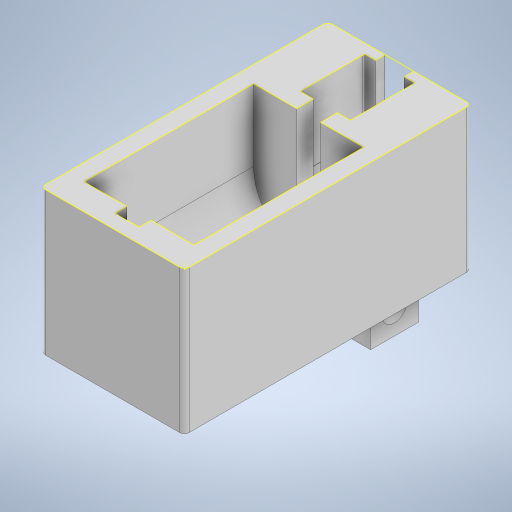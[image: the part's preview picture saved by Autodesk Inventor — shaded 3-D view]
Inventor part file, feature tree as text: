
AUTODESK INVENTOR PART (.ipt)
format: ipt  version: 2023 (Build 270158000, 158)  size: 730,624 bytes
history: native  units: in
note: dims shown in document units (in); Inventor stores cm internally (conversion verified against a paired STEP export)
features: extrude x17, sketch x15, plane x9, projected_geometry x4, fillet x3, chamfer x3
ambient origin geometry x8: Origin, YZ Plane, XZ Plane, XY Plane, X Axis, Y Axis, Z Axis, Center Point
bodies: Solid1 (feature_tree)
feature tree (51):
  sketch  "Sketch1"  dims[d0=2.3622in d1=4.7244in d2=1.7717in d3=0.1969in d4=0.9843in d5=0.0394in d6=0.4921in d7=0.3937in d8=0.0984in d9=0.8858in d10=-2.7165in d11=0.9843in d12=90.0deg d13=0.8268in d14=0.1969in d15=0.3937in d16=90.0deg d17=0.3937in d18=-2.7165in d19=90.0deg d20=-1.3583in d21=1.7717in d22=2.3622in d23=0.0in]
  extrude  "Extrusion1"  Depth=2.3622in TaperAngle=0.0deg
  sketch  "Sketch2"  dims[d24=-0.1969in d25=0.8268in]
  plane  "Work Plane1"
  plane  "Work Plane2"
  plane  "Work Plane3"
  plane  "Work Plane5"
  sketch  "Sketch3"  dims[d28=0.3937in d29=0.0in d30=0.3937in]
  plane  "Work Plane6"
  extrude  "Extrusion3"  Depth=0.8268in
  sketch  "Sketch4"  dims[d31=1.811in d32=0.3937in d33=0.0in]
  sketch  "Sketch5"  dims[d34=0.3937in d35=0.0in d36=0.3937in d37=0.0in]
  extrude  "Extrusion4"  Depth=0.3937in
  plane  "Work Plane7"
  extrude  "Extrusion5"  Depth=0.3937in TaperAngle=0.0deg
  extrude  "Extrusion6"  Depth=0.3937in TaperAngle=0.0deg
  extrude  "Extrusion7"  Depth=0.3937in TaperAngle=0.0deg
  fillet  "Fillet1"  Radius=0.0787in
  extrude  "Extrusion8"  Depth=0.3937in
  chamfer  "Chamfer1"  [1 undecoded]
  chamfer  "Chamfer2"  Distance=0.0787in Angle=45.0deg
  fillet  "Fillet2"  Radius=0.0394in
  fillet  "Fillet3"  Radius=0.0394in
  extrude  "Extrusion11"  Depth=0.3937in
  extrude  "Extrusion12"  Depth=0.3937in
  extrude  "Extrusion13"  Depth=0.3937in TaperAngle=0.0deg
  chamfer  "Chamfer3"  [1 undecoded]
  plane  "Work Plane8"
  extrude  "Extrusion14"  Depth=0.0787in
  extrude  "Extrusion15"  Depth=0.1969in
  extrude  "Extrusion16"  Depth=0.3937in TaperAngle=0.0deg
  extrude  "Extrusion17"  Depth=0.3937in
  extrude  "Extrusion19"  Depth=0.2362in
  extrude  "Extrusion20"  Depth=0.3937in TaperAngle=0.0deg
  plane  "Work Plane9"
  extrude  "Extrusion21"  Depth=0.1969in TaperAngle=0.0deg
  sketch  "Sketch17"  dims[d90=0.1575in d91=0.7874in d92=0.0in d93=0.481in d95=0.2362in d96=0.6299in d97=0.0in d98=0.1969in d99=0.0in d100=0.0197in d101=0.0197in d102=0.1969in d103=0.0in d104=0.0787in d107=0.3937in d108=0.0in d112=0.0394in d113=0.0394in d114=0.0394in d115=0.0394in d116=0.0in d117=0.0in d118=-0.0394in d119=0.3937in d120=0.0in]
  projected_geometry  "Projected Loop1"
  plane  "Work Plane4"
  sketch  "Sketch7"  dims[d38=-0.0787in d39=0.3937in d40=0.0in d41=0.0787in]
  sketch  "Sketch8"  dims[d42=0.3937in d43=0.3937in d44=0.0in d45=0.0in d46=0.0787in d47=0.0787in d48=45.0deg]
  sketch  "Sketch9"  dims[d49=0.0787in d50=0.0787in d51=45.0deg d52=0.0394in d53=0.0394in]
  sketch  "Sketch11"  dims[d69=0.3937in d70=0.0in d72=0.315in]
  sketch  "Sketch12"  dims[d74=0.7874in d75=0.3937in]
  sketch  "Sketch13"  dims[d76=0.3937in d79=0.7874in d80=0.0in]
  sketch  "Sketch14"  dims[d81=0.2559in d82=0.0in d83=0.0in]
  sketch  "Sketch15"  dims[d84=0.0787in d85=0.0787in d86=45.0deg d87=0.6299in]
  projected_geometry  "Projected Loop3"
  sketch  "Sketch16"  dims[d88=-1.1811in d89=0.1969in]
  projected_geometry  "Projected Loop4"
  projected_geometry  "Projected Loop5"
note: 2 required parameter values undecoded (feature->parameter linkage not recoverable at this tier; creation-order binding heuristic only, values carry confidence <= 0.55)
